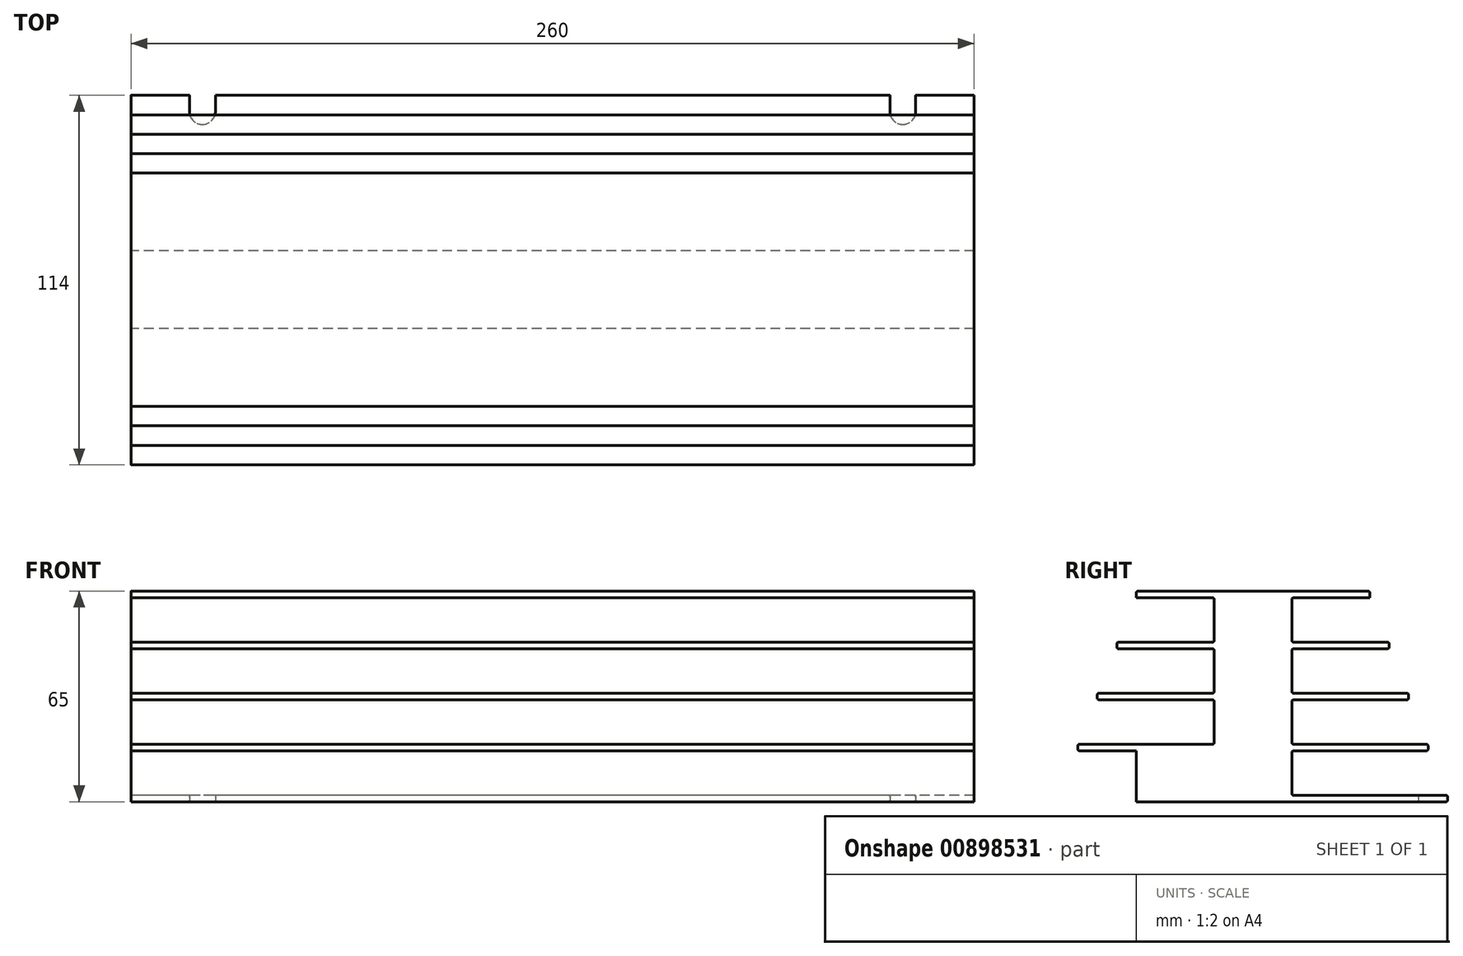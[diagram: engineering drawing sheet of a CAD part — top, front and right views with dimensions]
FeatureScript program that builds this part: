
annotation { "Feature Type Name" : "Feature", "Feature Type Description" : "" }
export const myFeature = defineFeature(function(context is Context, id is Id, definition is map)
    precondition{}
    {
        {
            var Q0;
            Q0=qCreatedBy(makeId("Top.planeOp"),FACE);
            var sketch = newSketch(context, id + "F0", { "sketchPlane" : qUnion([Q0])});
            skLineSegment(sketch, "E0.top", {"start": v(130, 60) * mm, "end": v(-130, 60) * mm});
            skPoint(sketch, "E0.middle", {"position": v(0, 0) * mm});
            skLineSegment(sketch, "E1", {"start": v(130, -60) * mm, "end": v(130, -36) * mm});
            skLineSegment(sketch, "E2", {"start": v(130, -36) * mm, "end": v(130, -12) * mm});
            skLineSegment(sketch, "E3", {"start": v(130, 12) * mm, "end": v(130, -12) * mm});
            skLineSegment(sketch, "E4", {"start": v(130, 12) * mm, "end": v(130, 36) * mm});
            skLineSegment(sketch, "E5", {"start": v(130, 60) * mm, "end": v(130, 36) * mm});
            skLineSegment(sketch, "E6.bottom", {"start": v(130, -36) * mm, "end": v(-130, -36) * mm});
            skLineSegment(sketch, "E6.left", {"start": v(130, -36) * mm, "end": v(130, -60) * mm});
            skLineSegment(sketch, "E6.right", {"start": v(-130, -36) * mm, "end": v(-130, -60) * mm});
            skLineSegment(sketch, "E7.bottom", {"start": v(130, -12) * mm, "end": v(-130, -12) * mm});
            skLineSegment(sketch, "E7.left", {"start": v(130, -12) * mm, "end": v(130, -36) * mm});
            skLineSegment(sketch, "E7.right", {"start": v(-130, -12) * mm, "end": v(-130, -36) * mm});
            skLineSegment(sketch, "E8.bottom", {"start": v(130, 12) * mm, "end": v(-130, 12) * mm});
            skLineSegment(sketch, "E8.right", {"start": v(-130, 12) * mm, "end": v(-130, -12) * mm});
            skLineSegment(sketch, "E9.bottom", {"start": v(130, 36) * mm, "end": v(-130, 36) * mm});
            skLineSegment(sketch, "E9.left", {"start": v(130, 36) * mm, "end": v(130, 12) * mm});
            skLineSegment(sketch, "E9.right", {"start": v(-130, 36) * mm, "end": v(-130, 12) * mm});
            skLineSegment(sketch, "E10", {"start": v(-130, 36) * mm, "end": v(-130, 60) * mm});
            skLineSegment(sketch, "E11", {"start": v(-130, -60) * mm, "end": v(130, -60) * mm});
            skSolve(sketch);
        }
        {
            var Q0;
            Q0=makeQuery(id+"F0.imprint","IMPRINT",FACE,{"disambiguationData":[TD([[makeQuery(id+"F0.imprint","IMPRINT",EDGE,{"derivedFrom":sQuery(id+"F0.wireOp",EDGE,"E6.bottom")}),-1.0]])]});
            var Q1;
            Q1=makeQuery(id+"F0.imprint","IMPRINT",FACE,{"disambiguationData":[TD([[makeQuery(id+"F0.imprint","IMPRINT",EDGE,{"derivedFrom":sQuery(id+"F0.wireOp",EDGE,"E7.bottom")}),-1.0]])]});
            var Q2;
            Q2=makeQuery(id+"F0.imprint","IMPRINT",FACE,{"disambiguationData":[TD([[makeQuery(id+"F0.imprint","IMPRINT",EDGE,{"derivedFrom":sQuery(id+"F0.wireOp",EDGE,"E9.bottom")}),1.0]])]});
            extrude(context, id + "F1", {"entities" : qUnion([Q0, Q1, Q2]), "depth" : 65 * mm, "offsetDistance" : 25 * mm});
        }
        {
            var Q0;
            Q0=makeQuery(id+"F0.imprint","IMPRINT",FACE,{"disambiguationData":[TD([[makeQuery(id+"F0.imprint","IMPRINT",EDGE,{"derivedFrom":sQuery(id+"F0.wireOp",EDGE,"E6.left")}),-1.0]])]});
            var Q1;
            Q1=makeQuery(id+"F0.imprint","IMPRINT",FACE,{"disambiguationData":[TD([[makeQuery(id+"F0.imprint","IMPRINT",EDGE,{"derivedFrom":sQuery(id+"F0.wireOp",EDGE,"E0.top")}),1.0]])]});
            extrude(context, id + "F2", {"entities" : qUnion([Q0, Q1]), "operationType" : NewBodyOperationType.ADD, "depth" : 2 * mm, "offsetDistance" : 25 * mm});
        }
        {
            var Q0;
            Q0=makeQuery(id+"F2.boolean.opBoolean","MERGE",FACE,{"derivedFrom":[makeQuery(id+"F1.opExtrude","SWEPT_FACE",FACE,{"disambiguationData":[OSD([sQuery(id+"F0.wireOp",EDGE,"E7.right"),sQuery(id+"F0.wireOp",EDGE,"E8.right"),sQuery(id+"F0.wireOp",EDGE,"E9.right")])]}),makeQuery(id+"F2.opExtrude","SWEPT_FACE",FACE,{"disambiguationData":[OSD([sQuery(id+"F0.wireOp",EDGE,"E6.right")])]}),makeQuery(id+"F2.opExtrude","SWEPT_FACE",FACE,{"disambiguationData":[OSD([sQuery(id+"F0.wireOp",EDGE,"E10")])]})]});
            var sketch = newSketch(context, id + "F3", { "sketchPlane" : qUnion([Q0])});
            skLineSegment(sketch, "E12", {"start": v(-36, 65) * mm, "end": v(-36, 63) * mm});
            skLineSegment(sketch, "E13", {"start": v(-36, 63) * mm, "end": v(-12, 63) * mm});
            skLineSegment(sketch, "E14", {"start": v(-12, 2) * mm, "end": v(-36, 2) * mm});
            skLineSegment(sketch, "E15", {"start": v(0, 65) * mm, "end": v(0, 0) * mm});
            skPoint(sketch, "E16.endSnap0", {"position": v(0, 32.5) * mm});
            skLineSegment(sketch, "E17", {"start": v(-36, 2) * mm, "end": v(-60, 2) * mm});
            skLineSegment(sketch, "E18", {"start": v(-36, 65) * mm, "end": v(0, 65) * mm});
            skLineSegment(sketch, "E19", {"start": v(-60, 0) * mm, "end": v(-60, 2) * mm});
            skLineSegment(sketch, "E20", {"start": v(-60, 0) * mm, "end": v(0, 0) * mm});
            skLineSegment(sketch, "E21", {"start": v(-36, 65) * mm, "end": v(-42, 49.25) * mm});
            skLineSegment(sketch, "E22.left", {"start": v(-12, 63) * mm, "end": v(-12, 49.25) * mm});
            skLineSegment(sketch, "E23.left", {"start": v(-12, 2) * mm, "end": v(-12, 15.75) * mm});
            skLineSegment(sketch, "E24.bottom", {"start": v(-12, 49.25) * mm, "end": v(-42, 49.25) * mm});
            skLineSegment(sketch, "E25.left", {"start": v(-12, 47.25) * mm, "end": v(-12, 33.5) * mm});
            skLineSegment(sketch, "E26.bottom", {"start": v(-12, 33.5) * mm, "end": v(-48, 33.5) * mm});
            skLineSegment(sketch, "E27", {"start": v(-42, 49.25) * mm, "end": v(-48, 33.5) * mm});
            skLineSegment(sketch, "E28", {"start": v(-48, 33.5) * mm, "end": v(-54, 17.75) * mm});
            skLineSegment(sketch, "E29", {"start": v(-54, 17.75) * mm, "end": v(-60, 2) * mm});
            skLineSegment(sketch, "E30", {"start": v(-54, 17.75) * mm, "end": v(-54, 15.75) * mm});
            skLineSegment(sketch, "E31", {"start": v(-48, 33.5) * mm, "end": v(-48, 31.5) * mm});
            skLineSegment(sketch, "E32", {"start": v(-42, 49.25) * mm, "end": v(-42, 47.25) * mm});
            skLineSegment(sketch, "E33", {"start": v(-12, 17.75) * mm, "end": v(-12, 31.5) * mm});
            skLineSegment(sketch, "E34", {"start": v(-60, 2) * mm, "end": v(-12, 2) * mm});
            skLineSegment(sketch, "E35", {"start": v(-54, 15.75) * mm, "end": v(-12, 15.75) * mm});
            skLineSegment(sketch, "E36", {"start": v(-54, 17.75) * mm, "end": v(-12, 17.75) * mm});
            skLineSegment(sketch, "E37", {"start": v(-48, 31.5) * mm, "end": v(-12, 31.5) * mm});
            skLineSegment(sketch, "E38", {"start": v(-42, 47.25) * mm, "end": v(-12, 47.25) * mm});
            skLineSegment(sketch, "E39.MirrorCS", {"start": v(48, 33.5) * mm, "end": v(48, 31.5) * mm});
            skLineSegment(sketch, "E40.MirrorCS", {"start": v(42, 49.25) * mm, "end": v(42, 47.25) * mm});
            skLineSegment(sketch, "E41.MirrorCS", {"start": v(60, 0) * mm, "end": v(60, 2) * mm});
            skLineSegment(sketch, "E42.MirrorCS", {"start": v(54, 17.75) * mm, "end": v(54, 15.75) * mm});
            skLineSegment(sketch, "E43.MirrorCS", {"start": v(36, 65) * mm, "end": v(36, 63) * mm});
            skLineSegment(sketch, "E44.MirrorCS", {"start": v(60, 2) * mm, "end": v(12, 2) * mm});
            skLineSegment(sketch, "E45.MirrorCS", {"start": v(54, 17.75) * mm, "end": v(12, 17.75) * mm});
            skLineSegment(sketch, "E46.MirrorCS", {"start": v(42, 49.25) * mm, "end": v(48, 33.5) * mm});
            skLineSegment(sketch, "E47.MirrorCS", {"start": v(48, 31.5) * mm, "end": v(12, 31.5) * mm});
            skLineSegment(sketch, "E48.MirrorCS", {"start": v(54, 17.75) * mm, "end": v(60, 2) * mm});
            skLineSegment(sketch, "E49.MirrorCS", {"start": v(12, 33.5) * mm, "end": v(48, 33.5) * mm});
            skLineSegment(sketch, "E50.MirrorCS", {"start": v(12, 2) * mm, "end": v(36, 2) * mm});
            skLineSegment(sketch, "E51.MirrorCS", {"start": v(36, 63) * mm, "end": v(12, 63) * mm});
            skLineSegment(sketch, "E52.MirrorCS", {"start": v(36, 65) * mm, "end": v(42, 49.25) * mm});
            skLineSegment(sketch, "E53.MirrorCS", {"start": v(36, 2) * mm, "end": v(60, 2) * mm});
            skLineSegment(sketch, "E54.MirrorCS", {"start": v(12, 49.25) * mm, "end": v(42, 49.25) * mm});
            skLineSegment(sketch, "E55.MirrorCS", {"start": v(12, 47.25) * mm, "end": v(12, 33.5) * mm});
            skLineSegment(sketch, "E56.MirrorCS", {"start": v(54, 15.75) * mm, "end": v(12, 15.75) * mm});
            skLineSegment(sketch, "E57.MirrorCS", {"start": v(12, 17.75) * mm, "end": v(12, 31.5) * mm});
            skLineSegment(sketch, "E58.MirrorCS", {"start": v(42, 47.25) * mm, "end": v(12, 47.25) * mm});
            skLineSegment(sketch, "E59.MirrorCS", {"start": v(12, 2) * mm, "end": v(12, 15.75) * mm});
            skLineSegment(sketch, "E60.MirrorCS", {"start": v(12, 63) * mm, "end": v(12, 49.25) * mm});
            skLineSegment(sketch, "E61.MirrorCS", {"start": v(60, 0) * mm, "end": v(0, 0) * mm});
            skLineSegment(sketch, "E62.MirrorCS", {"start": v(36, 65) * mm, "end": v(0, 65) * mm});
            skLineSegment(sketch, "E63.MirrorCS", {"start": v(48, 33.5) * mm, "end": v(54, 17.75) * mm});
            skSolve(sketch);
        }
        {
            var Q0;
            {var subQ0=sQuery(id+"F3.wireOp",EDGE,"VOB44XC7-ClNw-GyMX-yhTf-OrOPW011rkf9.bottom");Q0=makeQuery(id+"F3.imprint","IMPRINT",FACE,{"disambiguationData":[TD([[makeQuery(id+"F3.imprint","IMPRINT",EDGE,{"derivedFrom":subQ0}),-1.0]])]});}
            var Q1;
            {var subQ0=sQuery(id+"F3.wireOp",EDGE,"ddmvhHAo-rXDF-oPt6-O0bK-fkdRGT4dBXbs.bottom");Q1=makeQuery(id+"F3.imprint","IMPRINT",FACE,{"disambiguationData":[TD([[makeQuery(id+"F3.imprint","IMPRINT",EDGE,{"derivedFrom":subQ0}),-1.0]])]});}
            var Q2;
            {var subQ0=sQuery(id+"F3.wireOp",EDGE,"Rl54tbqv-DGgJ-5LB0-7HWp-a68NYDBfs7nv.bottom");Q2=makeQuery(id+"F3.imprint","IMPRINT",FACE,{"disambiguationData":[TD([[makeQuery(id+"F3.imprint","IMPRINT",EDGE,{"derivedFrom":subQ0}),-1.0]])]});}
            var Q3;
            {var subQ0=sQuery(id+"F3.wireOp",EDGE,"8fb58ea3-9cae-4c41-9406-59adf56fdd920.MirrorCS");Q3=makeQuery(id+"F3.imprint","IMPRINT",FACE,{"disambiguationData":[TD([[makeQuery(id+"F3.imprint","IMPRINT",EDGE,{"derivedFrom":subQ0}),1.0]])]});}
            var Q4;
            {var subQ0=sQuery(id+"F3.wireOp",EDGE,"b83053a2-9651-4f4e-9230-658251ae384a0.MirrorCS");Q4=makeQuery(id+"F3.imprint","IMPRINT",FACE,{"disambiguationData":[TD([[makeQuery(id+"F3.imprint","IMPRINT",EDGE,{"derivedFrom":subQ0}),-1.0]])]});}
            var Q5;
            {var subQ0=sQuery(id+"F3.wireOp",EDGE,"5c6d1357-a55f-4c19-ab3b-0d35c128dfcc0.MirrorCS");Q5=makeQuery(id+"F3.imprint","IMPRINT",FACE,{"disambiguationData":[TD([[makeQuery(id+"F3.imprint","IMPRINT",EDGE,{"derivedFrom":subQ0}),-1.0]])]});}
            var Q6;
            Q6=makeQuery(id+"F3.imprint","IMPRINT",FACE,{"disambiguationData":[TD([[makeQuery(id+"F3.imprint","IMPRINT",EDGE,{"derivedFrom":sQuery(id+"F3.wireOp",EDGE,"E15")}),1.0]])]});
            var Q7;
            Q7=makeQuery(id+"F3.imprint","IMPRINT",FACE,{"disambiguationData":[TD([[makeQuery(id+"F3.imprint","IMPRINT",EDGE,{"derivedFrom":sQuery(id+"F3.wireOp",EDGE,"E12")}),1.0]])]});
            var Q8;
            {var subQ0=sQuery(id+"F3.wireOp",EDGE,"E31");Q8=makeQuery(id+"F3.imprint","IMPRINT",FACE,{"disambiguationData":[TD([[makeQuery(id+"F3.imprint","IMPRINT",EDGE,{"derivedFrom":subQ0}),1.0]])]});}
            var Q9;
            {var subQ0=sQuery(id+"F3.wireOp",EDGE,"E32");Q9=makeQuery(id+"F3.imprint","IMPRINT",FACE,{"disambiguationData":[TD([[makeQuery(id+"F3.imprint","IMPRINT",EDGE,{"derivedFrom":subQ0}),1.0]])]});}
            var Q10;
            {var subQ0=sQuery(id+"F3.wireOp",EDGE,"E30");Q10=makeQuery(id+"F3.imprint","IMPRINT",FACE,{"disambiguationData":[TD([[makeQuery(id+"F3.imprint","IMPRINT",EDGE,{"derivedFrom":subQ0}),1.0]])]});}
            var Q11;
            {var subQ0=sQuery(id+"F3.wireOp",EDGE,"E42.MirrorCS");Q11=makeQuery(id+"F3.imprint","IMPRINT",FACE,{"disambiguationData":[TD([[makeQuery(id+"F3.imprint","IMPRINT",EDGE,{"derivedFrom":subQ0}),-1.0]])]});}
            var Q12;
            {var subQ0=sQuery(id+"F3.wireOp",EDGE,"E39.MirrorCS");Q12=makeQuery(id+"F3.imprint","IMPRINT",FACE,{"disambiguationData":[TD([[makeQuery(id+"F3.imprint","IMPRINT",EDGE,{"derivedFrom":subQ0}),-1.0]])]});}
            var Q13;
            {var subQ0=sQuery(id+"F3.wireOp",EDGE,"E40.MirrorCS");Q13=makeQuery(id+"F3.imprint","IMPRINT",FACE,{"disambiguationData":[TD([[makeQuery(id+"F3.imprint","IMPRINT",EDGE,{"derivedFrom":subQ0}),-1.0]])]});}
            extrude(context, id + "F4", {"entities" : qUnion([Q0, Q1, Q2, Q3, Q4, Q5, Q6, Q7, Q8, Q9, Q10, Q11, Q12, Q13]), "operationType" : NewBodyOperationType.ADD, "oppositeDirection" : true, "depth" : 260 * mm, "offsetDistance" : 25 * mm});
        }
        {
            var Q0;
            {var subQ0=sQuery(id+"F3.wireOp",EDGE,"E14");Q0=makeQuery(id+"F3.imprint","IMPRINT",FACE,{"disambiguationData":[TD([[makeQuery(id+"F3.imprint","IMPRINT",EDGE,{"derivedFrom":subQ0}),-1.0]])]});}
            var Q1;
            {var subQ0=sQuery(id+"F3.wireOp",EDGE,"E16");Q1=makeQuery(id+"F3.imprint","IMPRINT",FACE,{"disambiguationData":[TD([[makeQuery(id+"F3.imprint","IMPRINT",EDGE,{"derivedFrom":subQ0}),-1.0]])]});}
            var Q2;
            {var subQ0=sQuery(id+"F3.wireOp",EDGE,"NHxaGBeV-4gtu-DKFp-iAaf-ck9IbSCxoZdo");Q2=makeQuery(id+"F3.imprint","IMPRINT",FACE,{"disambiguationData":[TD([[makeQuery(id+"F3.imprint","IMPRINT",EDGE,{"derivedFrom":subQ0}),-1.0]])]});}
            var Q3;
            {var subQ0=sQuery(id+"F3.wireOp",EDGE,"E13");Q3=makeQuery(id+"F3.imprint","IMPRINT",FACE,{"disambiguationData":[TD([[makeQuery(id+"F3.imprint","IMPRINT",EDGE,{"derivedFrom":subQ0}),-1.0]])]});}
            var Q4;
            {var subQ0=sQuery(id+"F3.wireOp",EDGE,"cff9b413-af6f-4f54-9000-b51f28820bbb0.MirrorCS");Q4=makeQuery(id+"F3.imprint","IMPRINT",FACE,{"disambiguationData":[TD([[makeQuery(id+"F3.imprint","IMPRINT",EDGE,{"derivedFrom":subQ0}),1.0]])]});}
            var Q5;
            {var subQ0=sQuery(id+"F3.wireOp",EDGE,"052e5a8e-2220-40cd-bb55-0808d8f30db30.MirrorCS");Q5=makeQuery(id+"F3.imprint","IMPRINT",FACE,{"disambiguationData":[TD([[makeQuery(id+"F3.imprint","IMPRINT",EDGE,{"derivedFrom":subQ0}),1.0]])]});}
            var Q6;
            {var subQ0=sQuery(id+"F3.wireOp",EDGE,"160a3103-f72d-4168-85d9-5d2f4bcd6eef0.MirrorCS");Q6=makeQuery(id+"F3.imprint","IMPRINT",FACE,{"disambiguationData":[TD([[makeQuery(id+"F3.imprint","IMPRINT",EDGE,{"derivedFrom":subQ0}),1.0]])]});}
            var Q7;
            Q7=makeQuery(id+"F3.imprint","IMPRINT",FACE,{"disambiguationData":[TD([[makeQuery(id+"F3.imprint","IMPRINT",EDGE,{"derivedFrom":sQuery(id+"F3.wireOp",EDGE,"3a831cba-d87e-4c68-ab0b-4a3b8184c33a0.MirrorCS")}),1.0]])]});
            var Q8;
            {var subQ0=sQuery(id+"F3.wireOp",EDGE,"E25.left");Q8=makeQuery(id+"F3.imprint","IMPRINT",FACE,{"disambiguationData":[TD([[makeQuery(id+"F3.imprint","IMPRINT",EDGE,{"derivedFrom":subQ0}),-1.0]])]});}
            var Q9;
            {var subQ0=sQuery(id+"F3.wireOp",EDGE,"E33");Q9=makeQuery(id+"F3.imprint","IMPRINT",FACE,{"disambiguationData":[TD([[makeQuery(id+"F3.imprint","IMPRINT",EDGE,{"derivedFrom":subQ0}),1.0]])]});}
            var Q10;
            {var subQ0=sQuery(id+"F3.wireOp",EDGE,"E23.left");Q10=makeQuery(id+"F3.imprint","IMPRINT",FACE,{"disambiguationData":[TD([[makeQuery(id+"F3.imprint","IMPRINT",EDGE,{"derivedFrom":subQ0}),1.0]])]});}
            var Q11;
            {var subQ0=sQuery(id+"F3.wireOp",EDGE,"E50.MirrorCS");Q11=makeQuery(id+"F3.imprint","IMPRINT",FACE,{"disambiguationData":[TD([[makeQuery(id+"F3.imprint","IMPRINT",EDGE,{"derivedFrom":subQ0}),1.0]])]});}
            var Q12;
            {var subQ0=sQuery(id+"F3.wireOp",EDGE,"E57.MirrorCS");Q12=makeQuery(id+"F3.imprint","IMPRINT",FACE,{"disambiguationData":[TD([[makeQuery(id+"F3.imprint","IMPRINT",EDGE,{"derivedFrom":subQ0}),-1.0]])]});}
            var Q13;
            {var subQ0=sQuery(id+"F3.wireOp",EDGE,"E55.MirrorCS");Q13=makeQuery(id+"F3.imprint","IMPRINT",FACE,{"disambiguationData":[TD([[makeQuery(id+"F3.imprint","IMPRINT",EDGE,{"derivedFrom":subQ0}),1.0]])]});}
            var Q14;
            {var subQ0=sQuery(id+"F3.wireOp",EDGE,"E51.MirrorCS");Q14=makeQuery(id+"F3.imprint","IMPRINT",FACE,{"disambiguationData":[TD([[makeQuery(id+"F3.imprint","IMPRINT",EDGE,{"derivedFrom":subQ0}),1.0]])]});}
            extrude(context, id + "F5", {"entities" : qUnion([Q0, Q1, Q2, Q3, Q4, Q5, Q6, Q7, Q8, Q9, Q10, Q11, Q12, Q13, Q14]), "operationType" : NewBodyOperationType.REMOVE, "oppositeDirection" : true, "depth" : 260 * mm, "offsetDistance" : 25 * mm});
        }
        {
            var Q0;
            Q0=makeQuery(id+"F1.opExtrude","CAP_EDGE",EDGE,{"disambiguationData":[OSD([sQuery(id+"F0.wireOp",EDGE,"E9.bottom")])],"isStart":false});
            var Q1;
            Q1=makeQuery(id+"F5.boolean.opBoolean","COPY",EDGE,{"derivedFrom":makeQuery(id+"F5.opExtrude","SWEPT_EDGE",EDGE,{"disambiguationData":[OSD([sQuery(id+"F0.wireOp",EDGE,"E9.bottom"),sQuery(id+"F0.wireOp",EDGE,"E9.right"),sQuery(id+"F0.wireOp",EDGE,"E10"),sQuery(id+"F3.wireOp",EDGE,"E12"),sQuery(id+"F3.wireOp",EDGE,"E13")])]})});
            var Q2;
            Q2=makeQuery(id+"F4.opExtrude","SWEPT_EDGE",EDGE,{"disambiguationData":[OSD([sQuery(id+"F3.wireOp",EDGE,"E26.bottom"),sQuery(id+"F3.wireOp",EDGE,"E27"),sQuery(id+"F3.wireOp",EDGE,"E28"),sQuery(id+"F3.wireOp",EDGE,"E31")])]});
            var Q3;
            Q3=makeQuery(id+"F4.opExtrude","SWEPT_EDGE",EDGE,{"disambiguationData":[OSD([sQuery(id+"F3.wireOp",EDGE,"E31"),sQuery(id+"F3.wireOp",EDGE,"E37")])]});
            var Q4;
            Q4=makeQuery(id+"F4.opExtrude","SWEPT_EDGE",EDGE,{"disambiguationData":[OSD([sQuery(id+"F3.wireOp",EDGE,"E28"),sQuery(id+"F3.wireOp",EDGE,"E29"),sQuery(id+"F3.wireOp",EDGE,"E30"),sQuery(id+"F3.wireOp",EDGE,"E36")])]});
            var Q5;
            Q5=makeQuery(id+"F4.opExtrude","SWEPT_EDGE",EDGE,{"disambiguationData":[OSD([sQuery(id+"F3.wireOp",EDGE,"E30"),sQuery(id+"F3.wireOp",EDGE,"E35")])]});
            var Q6;
            Q6=makeQuery(id+"F2.opExtrude","CAP_EDGE",EDGE,{"disambiguationData":[OSD([sQuery(id+"F0.wireOp",EDGE,"E0.top")])],"isStart":true});
            var Q7;
            Q7=makeQuery(id+"F2.opExtrude","CAP_EDGE",EDGE,{"disambiguationData":[OSD([sQuery(id+"F0.wireOp",EDGE,"E0.top")])],"isStart":false});
            var Q8;
            Q8=makeQuery(id+"F2.opExtrude","CAP_EDGE",EDGE,{"disambiguationData":[OSD([sQuery(id+"F0.wireOp",EDGE,"E11")])],"isStart":false});
            var Q9;
            Q9=makeQuery(id+"F4.opExtrude","SWEPT_EDGE",EDGE,{"disambiguationData":[OSD([sQuery(id+"F3.wireOp",EDGE,"E42.MirrorCS"),sQuery(id+"F3.wireOp",EDGE,"E45.MirrorCS"),sQuery(id+"F3.wireOp",EDGE,"E48.MirrorCS"),sQuery(id+"F3.wireOp",EDGE,"E63.MirrorCS")])]});
            var Q10;
            Q10=makeQuery(id+"F4.opExtrude","SWEPT_EDGE",EDGE,{"disambiguationData":[OSD([sQuery(id+"F3.wireOp",EDGE,"E39.MirrorCS"),sQuery(id+"F3.wireOp",EDGE,"E46.MirrorCS"),sQuery(id+"F3.wireOp",EDGE,"E49.MirrorCS"),sQuery(id+"F3.wireOp",EDGE,"E63.MirrorCS")])]});
            var Q11;
            Q11=makeQuery(id+"F4.opExtrude","SWEPT_EDGE",EDGE,{"disambiguationData":[OSD([sQuery(id+"F3.wireOp",EDGE,"E40.MirrorCS"),sQuery(id+"F3.wireOp",EDGE,"E46.MirrorCS"),sQuery(id+"F3.wireOp",EDGE,"E52.MirrorCS"),sQuery(id+"F3.wireOp",EDGE,"E54.MirrorCS")])]});
            var Q12;
            Q12=makeQuery(id+"F1.opExtrude","CAP_EDGE",EDGE,{"disambiguationData":[OSD([sQuery(id+"F0.wireOp",EDGE,"E6.bottom")])],"isStart":false});
            var Q13;
            Q13=makeQuery(id+"F2.opExtrude","CAP_EDGE",EDGE,{"disambiguationData":[OSD([sQuery(id+"F0.wireOp",EDGE,"E11")])],"isStart":true});
            var Q14;
            Q14=makeQuery(id+"F4.opExtrude","SWEPT_EDGE",EDGE,{"disambiguationData":[OSD([sQuery(id+"F3.wireOp",EDGE,"E42.MirrorCS"),sQuery(id+"F3.wireOp",EDGE,"E56.MirrorCS")])]});
            var Q15;
            Q15=makeQuery(id+"F4.opExtrude","SWEPT_EDGE",EDGE,{"disambiguationData":[OSD([sQuery(id+"F3.wireOp",EDGE,"E39.MirrorCS"),sQuery(id+"F3.wireOp",EDGE,"E47.MirrorCS")])]});
            var Q16;
            Q16=makeQuery(id+"F4.opExtrude","SWEPT_EDGE",EDGE,{"disambiguationData":[OSD([sQuery(id+"F3.wireOp",EDGE,"E40.MirrorCS"),sQuery(id+"F3.wireOp",EDGE,"E58.MirrorCS")])]});
            var Q17;
            Q17=makeQuery(id+"F5.boolean.opBoolean","COPY",EDGE,{"derivedFrom":makeQuery(id+"F5.opExtrude","SWEPT_EDGE",EDGE,{"disambiguationData":[OSD([sQuery(id+"F0.wireOp",EDGE,"E6.right"),sQuery(id+"F0.wireOp",EDGE,"E6.bottom"),sQuery(id+"F0.wireOp",EDGE,"E7.right"),sQuery(id+"F3.wireOp",EDGE,"E43.MirrorCS"),sQuery(id+"F3.wireOp",EDGE,"E51.MirrorCS")])]})});
            var Q18;
            Q18=makeQuery(id+"F5.boolean.opBoolean","COPY",EDGE,{"derivedFrom":makeQuery(id+"F5.opExtrude","SWEPT_EDGE",EDGE,{"disambiguationData":[OSD([sQuery(id+"F3.wireOp",EDGE,"E13"),sQuery(id+"F3.wireOp",EDGE,"E22.left")])]})});
            var Q19;
            Q19=makeQuery(id+"F5.boolean.opBoolean","COPY",EDGE,{"derivedFrom":makeQuery(id+"F5.opExtrude","SWEPT_EDGE",EDGE,{"disambiguationData":[OSD([sQuery(id+"F3.wireOp",EDGE,"E22.left"),sQuery(id+"F3.wireOp",EDGE,"E24.bottom")])]})});
            var Q20;
            Q20=makeQuery(id+"F5.boolean.opBoolean","COPY",EDGE,{"derivedFrom":makeQuery(id+"F5.opExtrude","SWEPT_EDGE",EDGE,{"disambiguationData":[OSD([sQuery(id+"F3.wireOp",EDGE,"E25.left"),sQuery(id+"F3.wireOp",EDGE,"E26.bottom")])]})});
            var Q21;
            Q21=makeQuery(id+"F5.boolean.opBoolean","COPY",EDGE,{"derivedFrom":makeQuery(id+"F5.opExtrude","SWEPT_EDGE",EDGE,{"disambiguationData":[OSD([sQuery(id+"F3.wireOp",EDGE,"E25.left"),sQuery(id+"F3.wireOp",EDGE,"E38")])]})});
            var Q22;
            Q22=makeQuery(id+"F5.boolean.opBoolean","COPY",EDGE,{"derivedFrom":makeQuery(id+"F5.opExtrude","SWEPT_EDGE",EDGE,{"disambiguationData":[OSD([sQuery(id+"F3.wireOp",EDGE,"E33"),sQuery(id+"F3.wireOp",EDGE,"E37")])]})});
            var Q23;
            Q23=makeQuery(id+"F5.boolean.opBoolean","COPY",EDGE,{"derivedFrom":makeQuery(id+"F5.opExtrude","SWEPT_EDGE",EDGE,{"disambiguationData":[OSD([sQuery(id+"F3.wireOp",EDGE,"E23.left"),sQuery(id+"F3.wireOp",EDGE,"E35")])]})});
            var Q24;
            Q24=makeQuery(id+"F5.boolean.opBoolean","COPY",EDGE,{"derivedFrom":makeQuery(id+"F5.opExtrude","SWEPT_EDGE",EDGE,{"disambiguationData":[OSD([sQuery(id+"F3.wireOp",EDGE,"E23.left"),sQuery(id+"F3.wireOp",EDGE,"E34")])]})});
            var Q25;
            Q25=makeQuery(id+"F5.boolean.opBoolean","COPY",EDGE,{"derivedFrom":makeQuery(id+"F5.opExtrude","SWEPT_EDGE",EDGE,{"disambiguationData":[OSD([sQuery(id+"F3.wireOp",EDGE,"E51.MirrorCS"),sQuery(id+"F3.wireOp",EDGE,"E60.MirrorCS")])]})});
            var Q26;
            Q26=makeQuery(id+"F5.boolean.opBoolean","COPY",EDGE,{"derivedFrom":makeQuery(id+"F5.opExtrude","SWEPT_EDGE",EDGE,{"disambiguationData":[OSD([sQuery(id+"F3.wireOp",EDGE,"E55.MirrorCS"),sQuery(id+"F3.wireOp",EDGE,"E58.MirrorCS")])]})});
            var Q27;
            Q27=makeQuery(id+"F5.boolean.opBoolean","COPY",EDGE,{"derivedFrom":makeQuery(id+"F5.opExtrude","SWEPT_EDGE",EDGE,{"disambiguationData":[OSD([sQuery(id+"F3.wireOp",EDGE,"E47.MirrorCS"),sQuery(id+"F3.wireOp",EDGE,"E57.MirrorCS")])]})});
            var Q28;
            Q28=makeQuery(id+"F5.boolean.opBoolean","COPY",EDGE,{"derivedFrom":makeQuery(id+"F5.opExtrude","SWEPT_EDGE",EDGE,{"disambiguationData":[OSD([sQuery(id+"F3.wireOp",EDGE,"E54.MirrorCS"),sQuery(id+"F3.wireOp",EDGE,"E60.MirrorCS")])]})});
            var Q29;
            Q29=makeQuery(id+"F5.boolean.opBoolean","COPY",EDGE,{"derivedFrom":makeQuery(id+"F5.opExtrude","SWEPT_EDGE",EDGE,{"disambiguationData":[OSD([sQuery(id+"F3.wireOp",EDGE,"E49.MirrorCS"),sQuery(id+"F3.wireOp",EDGE,"E55.MirrorCS")])]})});
            var Q30;
            Q30=makeQuery(id+"F5.boolean.opBoolean","COPY",EDGE,{"derivedFrom":makeQuery(id+"F5.opExtrude","SWEPT_EDGE",EDGE,{"disambiguationData":[OSD([sQuery(id+"F3.wireOp",EDGE,"E56.MirrorCS"),sQuery(id+"F3.wireOp",EDGE,"E59.MirrorCS")])]})});
            var Q31;
            Q31=makeQuery(id+"F5.boolean.opBoolean","COPY",EDGE,{"derivedFrom":makeQuery(id+"F5.opExtrude","SWEPT_EDGE",EDGE,{"disambiguationData":[OSD([sQuery(id+"F3.wireOp",EDGE,"E45.MirrorCS"),sQuery(id+"F3.wireOp",EDGE,"E57.MirrorCS")])]})});
            var Q32;
            Q32=makeQuery(id+"F4.opExtrude","SWEPT_EDGE",EDGE,{"disambiguationData":[OSD([sQuery(id+"F3.wireOp",EDGE,"E21"),sQuery(id+"F3.wireOp",EDGE,"E24.bottom"),sQuery(id+"F3.wireOp",EDGE,"E27"),sQuery(id+"F3.wireOp",EDGE,"E32")])]});
            var Q33;
            Q33=makeQuery(id+"F5.boolean.opBoolean","COPY",EDGE,{"derivedFrom":makeQuery(id+"F5.opExtrude","SWEPT_EDGE",EDGE,{"disambiguationData":[OSD([sQuery(id+"F3.wireOp",EDGE,"E33"),sQuery(id+"F3.wireOp",EDGE,"E36")])]})});
            var Q34;
            Q34=makeQuery(id+"F5.boolean.opBoolean","COPY",EDGE,{"derivedFrom":makeQuery(id+"F5.opExtrude","SWEPT_EDGE",EDGE,{"disambiguationData":[OSD([sQuery(id+"F3.wireOp",EDGE,"E50.MirrorCS"),sQuery(id+"F3.wireOp",EDGE,"E59.MirrorCS")])]})});
            var Q35;
            Q35=makeQuery(id+"F4.opExtrude","SWEPT_EDGE",EDGE,{"disambiguationData":[OSD([sQuery(id+"F3.wireOp",EDGE,"E32"),sQuery(id+"F3.wireOp",EDGE,"E38")])]});
            fillet(context, id + "F6", {"entities" : qUnion([Q0, Q1, Q2, Q3, Q4, Q5, Q6, Q7, Q8, Q9, Q10, Q11, Q12, Q13, Q14, Q15, Q16, Q17, Q18, Q19, Q20, Q21, Q22, Q23, Q24, Q25, Q26, Q27, Q28, Q29, Q30, Q31, Q32, Q33, Q34, Q35]), "radius" : 0.5 * mm, "tangentPropagation" : true, "allowEdgeOverflow" : false});
        }
        {
            var Q0;
            {var subQ0=sQuery(id+"F0.wireOp",EDGE,"E6.bottom");var subQ1=sQuery(id+"F0.wireOp",EDGE,"E9.bottom");Q0=makeQuery(id+"F2.boolean.opBoolean","MERGE",FACE,{"derivedFrom":[makeQuery(id+"F1.opExtrude","CAP_FACE",FACE,{"disambiguationData":[OSD([subQ0,sQuery(id+"F0.wireOp",EDGE,"E7.left"),sQuery(id+"F0.wireOp",EDGE,"E7.right"),sQuery(id+"F0.wireOp",EDGE,"E3"),sQuery(id+"F0.wireOp",EDGE,"E8.right"),subQ1,sQuery(id+"F0.wireOp",EDGE,"E9.left"),sQuery(id+"F0.wireOp",EDGE,"E9.right")])],"isStart":true}),makeQuery(id+"F2.opExtrude","CAP_FACE",FACE,{"disambiguationData":[OSD([sQuery(id+"F0.wireOp",EDGE,"E0.top"),sQuery(id+"F0.wireOp",EDGE,"E5"),subQ1,sQuery(id+"F0.wireOp",EDGE,"E10")])],"isStart":true}),makeQuery(id+"F2.opExtrude","CAP_FACE",FACE,{"disambiguationData":[OSD([sQuery(id+"F0.wireOp",EDGE,"E6.left"),sQuery(id+"F0.wireOp",EDGE,"E6.right"),subQ0,sQuery(id+"F0.wireOp",EDGE,"E11")])],"isStart":true})]});}
            var sketch = newSketch(context, id + "F7", { "sketchPlane" : qUnion([Q0])});
            skLineSegment(sketch, "E64", {"start": v(-112, -60) * mm, "end": v(-112, -55) * mm});
            skLineSegment(sketch, "E65", {"start": v(-112, -55) * mm, "end": v(-104, -55) * mm});
            skArc(sketch, "E66", {"start": v(-112, -55) * mm, "mid": v(-108, -51) * mm, "end": v(-104, -55) * mm});
            skLineSegment(sketch, "E67", {"start": v(-104, -55) * mm, "end": v(-104, -60) * mm});
            skLineSegment(sketch, "E68", {"start": v(-104, -60) * mm, "end": v(-104, -55) * mm});
            skLineSegment(sketch, "E69", {"start": v(-112, -60) * mm, "end": v(-104, -60) * mm});
            skLineSegment(sketch, "E70.MirrorCS", {"start": v(-112, 60) * mm, "end": v(-104, 60) * mm});
            skLineSegment(sketch, "E71.MirrorCS", {"start": v(-112, 60) * mm, "end": v(-112, 55) * mm});
            skLineSegment(sketch, "E72.MirrorCS", {"start": v(-112, 55) * mm, "end": v(-104, 55) * mm});
            skArc(sketch, "E73.MirrorCS", {"start": v(-112, 55) * mm, "mid": v(-108, 51) * mm, "end": v(-104, 55) * mm});
            skLineSegment(sketch, "E74.MirrorCS", {"start": v(-104, 60) * mm, "end": v(-104, 55) * mm});
            skLineSegment(sketch, "E75.MirrorCS", {"start": v(104, -60) * mm, "end": v(104, -55) * mm});
            skLineSegment(sketch, "E76.MirrorCS", {"start": v(112, -60) * mm, "end": v(104, -60) * mm});
            skLineSegment(sketch, "E77.MirrorCS", {"start": v(112, -60) * mm, "end": v(112, -55) * mm});
            skLineSegment(sketch, "E78.MirrorCS", {"start": v(112, -55) * mm, "end": v(104, -55) * mm});
            skArc(sketch, "E79.MirrorCS", {"start": v(112, -55) * mm, "mid": v(108, -51) * mm, "end": v(104, -55) * mm});
            skLineSegment(sketch, "E80.MirrorCS", {"start": v(112, 60) * mm, "end": v(112, 55) * mm});
            skArc(sketch, "E81.MirrorCS", {"start": v(112, 55) * mm, "mid": v(108, 51) * mm, "end": v(104, 55) * mm});
            skLineSegment(sketch, "E82.MirrorCS", {"start": v(112, 55) * mm, "end": v(104, 55) * mm});
            skLineSegment(sketch, "E83.MirrorCS", {"start": v(104, 60) * mm, "end": v(104, 55) * mm});
            skLineSegment(sketch, "E84", {"start": v(104, 60) * mm, "end": v(112, 60) * mm});
            skLineSegment(sketch, "E85", {"start": v(104, -60) * mm, "end": v(112, -60) * mm});
            skSolve(sketch);
        }
        {
            var Q0;
            Q0=makeQuery(id+"F7.imprint","IMPRINT",FACE,{"disambiguationData":[TD([[makeQuery(id+"F7.imprint","IMPRINT",EDGE,{"derivedFrom":sQuery(id+"F7.wireOp",EDGE,"E64")}),-1.0]])]});
            var Q1;
            Q1=makeQuery(id+"F7.imprint","IMPRINT",FACE,{"disambiguationData":[TD([[makeQuery(id+"F7.imprint","IMPRINT",EDGE,{"derivedFrom":sQuery(id+"F7.wireOp",EDGE,"E65")}),1.0]])]});
            var Q2;
            Q2=makeQuery(id+"F7.imprint","IMPRINT",FACE,{"disambiguationData":[TD([[makeQuery(id+"F7.imprint","IMPRINT",EDGE,{"derivedFrom":sQuery(id+"F7.wireOp",EDGE,"E70.MirrorCS")}),-1.0]])]});
            var Q3;
            Q3=makeQuery(id+"F7.imprint","IMPRINT",FACE,{"disambiguationData":[TD([[makeQuery(id+"F7.imprint","IMPRINT",EDGE,{"derivedFrom":sQuery(id+"F7.wireOp",EDGE,"E72.MirrorCS")}),-1.0]])]});
            var Q4;
            Q4=makeQuery(id+"F7.imprint","IMPRINT",FACE,{"disambiguationData":[TD([[makeQuery(id+"F7.imprint","IMPRINT",EDGE,{"derivedFrom":sQuery(id+"F7.wireOp",EDGE,"E75.MirrorCS")}),-1.0]])]});
            var Q5;
            Q5=makeQuery(id+"F7.imprint","IMPRINT",FACE,{"disambiguationData":[TD([[makeQuery(id+"F7.imprint","IMPRINT",EDGE,{"derivedFrom":sQuery(id+"F7.wireOp",EDGE,"E78.MirrorCS")}),-1.0]])]});
            var Q6;
            Q6=makeQuery(id+"F7.imprint","IMPRINT",FACE,{"disambiguationData":[TD([[makeQuery(id+"F7.imprint","IMPRINT",EDGE,{"derivedFrom":sQuery(id+"F7.wireOp",EDGE,"E81.MirrorCS")}),-1.0]])]});
            var Q7;
            {var subQ0=sQuery(id+"F7.wireOp",EDGE,"E80.MirrorCS");Q7=makeQuery(id+"F7.imprint","IMPRINT",FACE,{"disambiguationData":[TD([[makeQuery(id+"F7.imprint","IMPRINT",EDGE,{"derivedFrom":subQ0}),-1.0]])]});}
            var Q8;
            {var subQ1=sQuery(id+"F7.wireOp",EDGE,"E72.MirrorCS");Q8=makeQuery(id+"F7.imprint","IMPRINT",FACE,{"disambiguationData":[TD([[makeQuery(id+"F7.imprint","IMPRINT",EDGE,{"derivedFrom":subQ1}),1.0]])]});}
            extrude(context, id + "F8", {"entities" : qUnion([Q0, Q1, Q2, Q3, Q4, Q5, Q6, Q7, Q8]), "operationType" : NewBodyOperationType.REMOVE, "oppositeDirection" : true, "depth" : 2 * mm, "offsetDistance" : 25 * mm});
        }
    });
